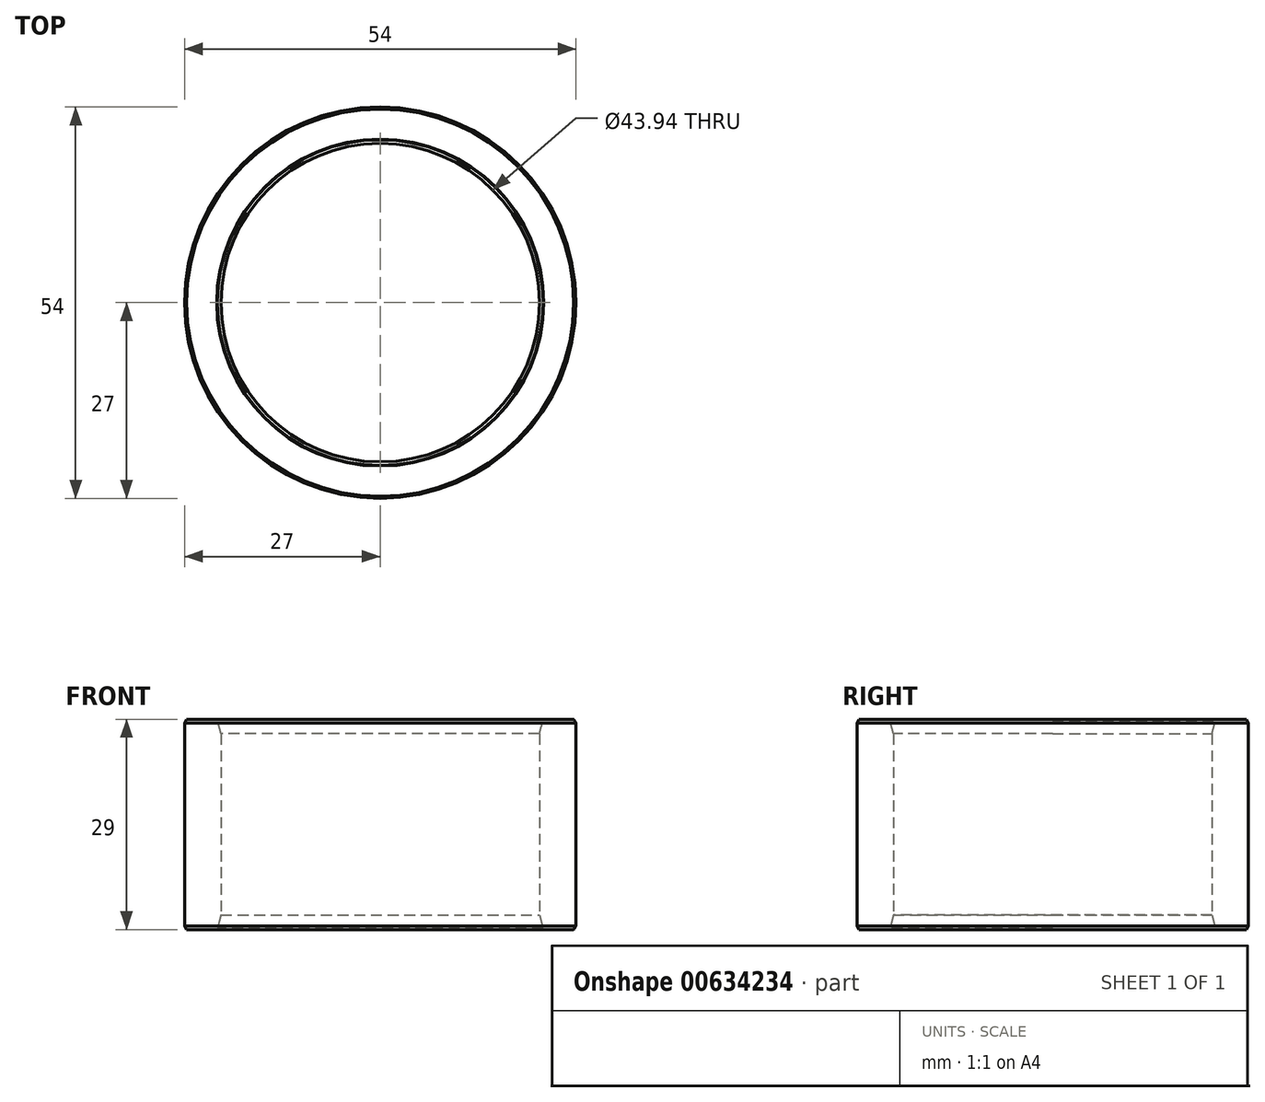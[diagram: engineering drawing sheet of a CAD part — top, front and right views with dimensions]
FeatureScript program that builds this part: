
annotation { "Feature Type Name" : "Feature", "Feature Type Description" : "" }
export const myFeature = defineFeature(function(context is Context, id is Id, definition is map)
    precondition{}
    {
        {
            var Q0;
            Q0=qCreatedBy(makeId("Top.planeOp"),FACE);
            var sketch = newSketch(context, id + "F0", { "sketchPlane" : qUnion([Q0])});
            skCircle(sketch, "E0", {"center": v(0, 0) * mm, "radius": 21.97 * mm});
            skCircle(sketch, "E1", {"center": v(0, 0) * mm, "radius": 27 * mm});
            skSolve(sketch);
        }
        {
            var Q0;
            Q0=makeQuery(id+"F0.imprint","IMPRINT",FACE,{"disambiguationData":[TD([[makeQuery(id+"F0.imprint","IMPRINT",EDGE,{"derivedFrom":sQuery(id+"F0.wireOp",EDGE,"E0")}),-1.0]])]});
            extrude(context, id + "F1", {"entities" : qUnion([Q0]), "depth" : 29 * mm, "offsetDistance" : 25 * mm});
        }
        {
            var Q0;
            Q0=makeQuery(id+"F1.opExtrude","CAP_EDGE",EDGE,{"disambiguationData":[OSD([sQuery(id+"F0.wireOp",EDGE,"E1")])],"isStart":false});
            var Q1;
            Q1=makeQuery(id+"F1.opExtrude","CAP_EDGE",EDGE,{"disambiguationData":[OSD([sQuery(id+"F0.wireOp",EDGE,"E1")])],"isStart":true});
            chamfer(context, id + "F2", {"entities" : qUnion([Q0, Q1]), "chamferType" : ChamferType.OFFSET_ANGLE, "width" : 0.5 * mm, "oppositeDirection" : true, "angle" : 30 * degree, "tangentPropagation" : true});
        }
        {
            var Q0;
            Q0=makeQuery(id+"F1.opExtrude","CAP_EDGE",EDGE,{"disambiguationData":[OSD([sQuery(id+"F0.wireOp",EDGE,"E0")])],"isStart":false});
            var Q1;
            Q1=makeQuery(id+"F1.opExtrude","CAP_EDGE",EDGE,{"disambiguationData":[OSD([sQuery(id+"F0.wireOp",EDGE,"E0")])],"isStart":true});
            chamfer(context, id + "F3", {"entities" : qUnion([Q0, Q1]), "chamferType" : ChamferType.OFFSET_ANGLE, "width" : 1 * mm, "oppositeDirection" : false, "angle" : 30 * degree});
        }
        {
            var Q0;
            {var subQ0=sQuery(id+"F0.wireOp",EDGE,"E0");Q0=makeQuery(id+"F3.opChamfer","BLEND_EDGE",EDGE,{"blendedFrom":[makeQuery(id+"F1.opExtrude","CAP_EDGE",EDGE,{"disambiguationData":[OSD([subQ0])],"isStart":false}),makeQuery(id+"F1.opExtrude","SWEPT_FACE",FACE,{"disambiguationData":[OSD([subQ0])]})],"blendedInto":[makeQuery(id+"F1.opExtrude","SWEPT_FACE",FACE,{"disambiguationData":[OSD([subQ0])]})]});}
            var Q1;
            {var subQ0=sQuery(id+"F0.wireOp",EDGE,"E0");Q1=makeQuery(id+"F3.opChamfer","BLEND_EDGE",EDGE,{"blendedFrom":[makeQuery(id+"F1.opExtrude","CAP_EDGE",EDGE,{"disambiguationData":[OSD([subQ0])],"isStart":true}),makeQuery(id+"F1.opExtrude","SWEPT_FACE",FACE,{"disambiguationData":[OSD([subQ0])]})],"blendedInto":[makeQuery(id+"F1.opExtrude","SWEPT_FACE",FACE,{"disambiguationData":[OSD([subQ0])]})]});}
            chamfer(context, id + "F4", {"entities" : qUnion([Q0, Q1]), "chamferType" : ChamferType.OFFSET_ANGLE, "width" : 1 * mm, "oppositeDirection" : false, "angle" : 15 * degree, "tangentPropagation" : true});
        }
    });
